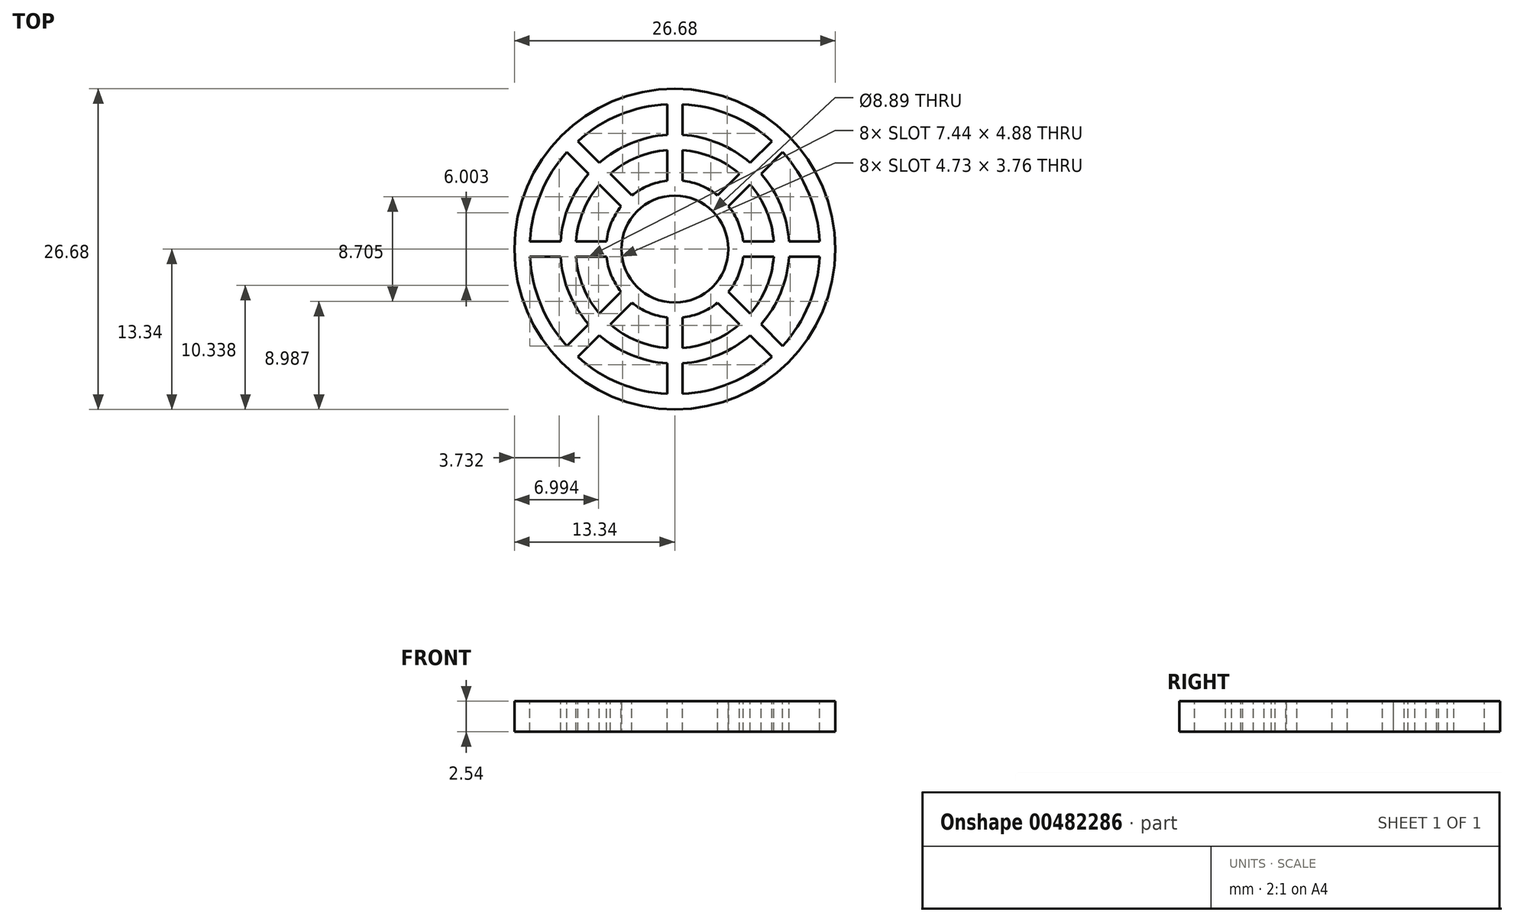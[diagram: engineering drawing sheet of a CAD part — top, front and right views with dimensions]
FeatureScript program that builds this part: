
annotation { "Feature Type Name" : "Feature", "Feature Type Description" : "" }
export const myFeature = defineFeature(function(context is Context, id is Id, definition is map)
    precondition{}
    {
        {
            var Q0;
            Q0=qCreatedBy(makeId("Top.planeOp"),FACE);
            var sketch = newSketch(context, id + "F0", { "sketchPlane" : qUnion([Q0])});
            skCircle(sketch, "E0", {"center": v(0, 0) * mm, "radius": 13.34 * mm});
            skCircle(sketch, "E1", {"center": v(0, 0) * mm, "radius": 4.45 * mm});
            skSolve(sketch);
        }
        {
            var Q0;
            Q0 = qSketchRegion(id + "F0", true);
            extrude(context, id + "F1", {"entities" : qUnion([Q0]), "depth" : 2.54 * mm});
        }
        {
            var Q0;
            Q0=makeQuery(id+"F1.opExtrude","CAP_FACE",FACE,{"disambiguationData":[OSD([sQuery(id+"F0.wireOp",EDGE,"E0"),sQuery(id+"F0.wireOp",EDGE,"E1")])],"isStart":false});
            var sketch = newSketch(context, id + "F2", { "sketchPlane" : qUnion([Q0])});
            skLineSegment(sketch, "E2", {"start": v(0, 0) * mm, "end": v(-9.43, -9.43) * mm, "construction": true});
            skArc(sketch, "E3", {"start": v(-3.57, -4.47) * mm, "mid": v(-2.19, -5.28) * mm, "end": v(-0.64, -5.68) * mm});
            skArc(sketch, "E4", {"start": v(-8.07, -8.97) * mm, "mid": v(-4.62, -11.15) * mm, "end": v(-0.64, -12.05) * mm});
            skLineSegment(sketch, "E5.trimOffspring", {"start": v(-3.57, -4.47) * mm, "end": v(-5.37, -6.27) * mm});
            skLineSegment(sketch, "E6.trimOffspring", {"start": v(-0.64, -5.68) * mm, "end": v(-0.63, -8.23) * mm});
            skArc(sketch, "E7.0", {"start": v(-5.82, -6.72) * mm, "mid": v(-3.4, -8.21) * mm, "end": v(-0.63, -8.86) * mm, "construction": true});
            skArc(sketch, "E8.0", {"start": v(-6.27, -7.17) * mm, "mid": v(-3.64, -8.8) * mm, "end": v(-0.64, -9.5) * mm});
            skArc(sketch, "E9.0", {"start": v(-5.37, -6.27) * mm, "mid": v(-3.16, -7.62) * mm, "end": v(-0.64, -8.23) * mm});
            skLineSegment(sketch, "E10.trimOffspring", {"start": v(-0.63, -9.5) * mm, "end": v(-0.63, -12.05) * mm});
            skLineSegment(sketch, "E11.trimOffspring", {"start": v(-6.27, -7.17) * mm, "end": v(-8.07, -8.97) * mm});
            skArc(sketch, "E12.1.0", {"start": v(0.64, -8.23) * mm, "mid": v(3.16, -7.62) * mm, "end": v(5.37, -6.27) * mm});
            skArc(sketch, "E12.1.1", {"start": v(0.64, -5.68) * mm, "mid": v(2.19, -5.28) * mm, "end": v(3.57, -4.47) * mm});
            skArc(sketch, "E12.1.2", {"start": v(0.63, -12.05) * mm, "mid": v(4.62, -11.15) * mm, "end": v(8.07, -8.97) * mm});
            skLineSegment(sketch, "E12.1.3", {"start": v(6.27, -7.17) * mm, "end": v(8.07, -8.97) * mm});
            skLineSegment(sketch, "E12.1.4", {"start": v(0.64, -9.5) * mm, "end": v(0.64, -12.05) * mm});
            skArc(sketch, "E12.1.5", {"start": v(0.64, -9.5) * mm, "mid": v(3.64, -8.8) * mm, "end": v(6.27, -7.17) * mm});
            skLineSegment(sketch, "E12.1.6", {"start": v(3.57, -4.47) * mm, "end": v(5.37, -6.27) * mm});
            skLineSegment(sketch, "E12.1.7", {"start": v(0.64, -5.68) * mm, "end": v(0.64, -8.23) * mm});
            skArc(sketch, "E12.2.0", {"start": v(6.27, -5.37) * mm, "mid": v(7.62, -3.16) * mm, "end": v(8.23, -0.64) * mm});
            skArc(sketch, "E12.2.1", {"start": v(4.47, -3.57) * mm, "mid": v(5.28, -2.19) * mm, "end": v(5.68, -0.64) * mm});
            skArc(sketch, "E12.2.2", {"start": v(8.97, -8.07) * mm, "mid": v(11.15, -4.62) * mm, "end": v(12.05, -0.64) * mm});
            skLineSegment(sketch, "E12.2.3", {"start": v(9.5, -0.64) * mm, "end": v(12.05, -0.64) * mm});
            skLineSegment(sketch, "E12.2.4", {"start": v(7.17, -6.27) * mm, "end": v(8.97, -8.07) * mm});
            skArc(sketch, "E12.2.5", {"start": v(7.17, -6.27) * mm, "mid": v(8.8, -3.64) * mm, "end": v(9.5, -0.64) * mm});
            skLineSegment(sketch, "E12.2.6", {"start": v(5.68, -0.64) * mm, "end": v(8.23, -0.64) * mm});
            skLineSegment(sketch, "E12.2.7", {"start": v(4.47, -3.57) * mm, "end": v(6.27, -5.37) * mm});
            skArc(sketch, "E12.3.0", {"start": v(8.23, 0.64) * mm, "mid": v(7.62, 3.16) * mm, "end": v(6.27, 5.37) * mm});
            skArc(sketch, "E12.3.1", {"start": v(5.68, 0.64) * mm, "mid": v(5.28, 2.19) * mm, "end": v(4.47, 3.57) * mm});
            skArc(sketch, "E12.3.2", {"start": v(12.05, 0.63) * mm, "mid": v(11.15, 4.62) * mm, "end": v(8.97, 8.07) * mm});
            skLineSegment(sketch, "E12.3.3", {"start": v(7.17, 6.27) * mm, "end": v(8.97, 8.07) * mm});
            skLineSegment(sketch, "E12.3.4", {"start": v(9.5, 0.64) * mm, "end": v(12.05, 0.64) * mm});
            skArc(sketch, "E12.3.5", {"start": v(9.5, 0.64) * mm, "mid": v(8.8, 3.64) * mm, "end": v(7.17, 6.27) * mm});
            skLineSegment(sketch, "E12.3.6", {"start": v(4.47, 3.57) * mm, "end": v(6.27, 5.37) * mm});
            skLineSegment(sketch, "E12.3.7", {"start": v(5.68, 0.64) * mm, "end": v(8.23, 0.64) * mm});
            skArc(sketch, "E12.4.0", {"start": v(5.37, 6.27) * mm, "mid": v(3.16, 7.62) * mm, "end": v(0.64, 8.23) * mm});
            skArc(sketch, "E12.4.1", {"start": v(3.57, 4.47) * mm, "mid": v(2.19, 5.28) * mm, "end": v(0.64, 5.68) * mm});
            skArc(sketch, "E12.4.2", {"start": v(8.07, 8.97) * mm, "mid": v(4.62, 11.15) * mm, "end": v(0.64, 12.05) * mm});
            skLineSegment(sketch, "E12.4.3", {"start": v(0.64, 9.5) * mm, "end": v(0.64, 12.05) * mm});
            skLineSegment(sketch, "E12.4.4", {"start": v(6.27, 7.17) * mm, "end": v(8.07, 8.97) * mm});
            skArc(sketch, "E12.4.5", {"start": v(6.27, 7.17) * mm, "mid": v(3.64, 8.8) * mm, "end": v(0.64, 9.5) * mm});
            skLineSegment(sketch, "E12.4.6", {"start": v(0.64, 5.68) * mm, "end": v(0.64, 8.23) * mm});
            skLineSegment(sketch, "E12.4.7", {"start": v(3.57, 4.47) * mm, "end": v(5.37, 6.27) * mm});
            skArc(sketch, "E12.5.0", {"start": v(-0.63, 8.23) * mm, "mid": v(-3.16, 7.62) * mm, "end": v(-5.37, 6.27) * mm});
            skArc(sketch, "E12.5.1", {"start": v(-0.64, 5.68) * mm, "mid": v(-2.19, 5.28) * mm, "end": v(-3.57, 4.47) * mm});
            skArc(sketch, "E12.5.2", {"start": v(-0.63, 12.05) * mm, "mid": v(-4.62, 11.15) * mm, "end": v(-8.07, 8.97) * mm});
            skLineSegment(sketch, "E12.5.3", {"start": v(-6.27, 7.17) * mm, "end": v(-8.07, 8.97) * mm});
            skLineSegment(sketch, "E12.5.4", {"start": v(-0.63, 9.5) * mm, "end": v(-0.63, 12.05) * mm});
            skArc(sketch, "E12.5.5", {"start": v(-0.63, 9.5) * mm, "mid": v(-3.64, 8.8) * mm, "end": v(-6.27, 7.17) * mm});
            skLineSegment(sketch, "E12.5.6", {"start": v(-3.57, 4.47) * mm, "end": v(-5.37, 6.27) * mm});
            skLineSegment(sketch, "E12.5.7", {"start": v(-0.64, 5.68) * mm, "end": v(-0.63, 8.23) * mm});
            skArc(sketch, "E12.6.0", {"start": v(-6.27, 5.37) * mm, "mid": v(-7.62, 3.16) * mm, "end": v(-8.23, 0.64) * mm});
            skArc(sketch, "E12.6.1", {"start": v(-4.47, 3.57) * mm, "mid": v(-5.28, 2.19) * mm, "end": v(-5.68, 0.64) * mm});
            skArc(sketch, "E12.6.2", {"start": v(-8.97, 8.07) * mm, "mid": v(-11.15, 4.62) * mm, "end": v(-12.05, 0.64) * mm});
            skLineSegment(sketch, "E12.6.3", {"start": v(-9.5, 0.64) * mm, "end": v(-12.05, 0.64) * mm});
            skLineSegment(sketch, "E12.6.4", {"start": v(-7.17, 6.27) * mm, "end": v(-8.97, 8.07) * mm});
            skArc(sketch, "E12.6.5", {"start": v(-7.17, 6.27) * mm, "mid": v(-8.8, 3.64) * mm, "end": v(-9.5, 0.64) * mm});
            skLineSegment(sketch, "E12.6.6", {"start": v(-5.68, 0.64) * mm, "end": v(-8.23, 0.64) * mm});
            skLineSegment(sketch, "E12.6.7", {"start": v(-4.47, 3.57) * mm, "end": v(-6.27, 5.37) * mm});
            skArc(sketch, "E12.7.0", {"start": v(-8.23, -0.63) * mm, "mid": v(-7.62, -3.16) * mm, "end": v(-6.27, -5.37) * mm});
            skArc(sketch, "E12.7.1", {"start": v(-5.68, -0.63) * mm, "mid": v(-5.28, -2.19) * mm, "end": v(-4.47, -3.57) * mm});
            skArc(sketch, "E12.7.2", {"start": v(-12.05, -0.63) * mm, "mid": v(-11.15, -4.62) * mm, "end": v(-8.97, -8.07) * mm});
            skLineSegment(sketch, "E12.7.3", {"start": v(-7.17, -6.27) * mm, "end": v(-8.97, -8.07) * mm});
            skLineSegment(sketch, "E12.7.4", {"start": v(-9.5, -0.63) * mm, "end": v(-12.05, -0.63) * mm});
            skArc(sketch, "E12.7.5", {"start": v(-9.5, -0.63) * mm, "mid": v(-8.8, -3.64) * mm, "end": v(-7.17, -6.27) * mm});
            skLineSegment(sketch, "E12.7.6", {"start": v(-4.47, -3.57) * mm, "end": v(-6.27, -5.37) * mm});
            skLineSegment(sketch, "E12.7.7", {"start": v(-5.68, -0.63) * mm, "end": v(-8.23, -0.63) * mm});
            skSolve(sketch);
        }
        {
            var Q0;
            Q0 = qSketchRegion(id + "F2", true);
            extrude(context, id + "F3", {"entities" : qUnion([Q0]), "operationType" : NewBodyOperationType.REMOVE, "endBound" : BoundingType.THROUGH_ALL, "oppositeDirection" : true, "depth" : 25.4 * mm});
        }
    });
